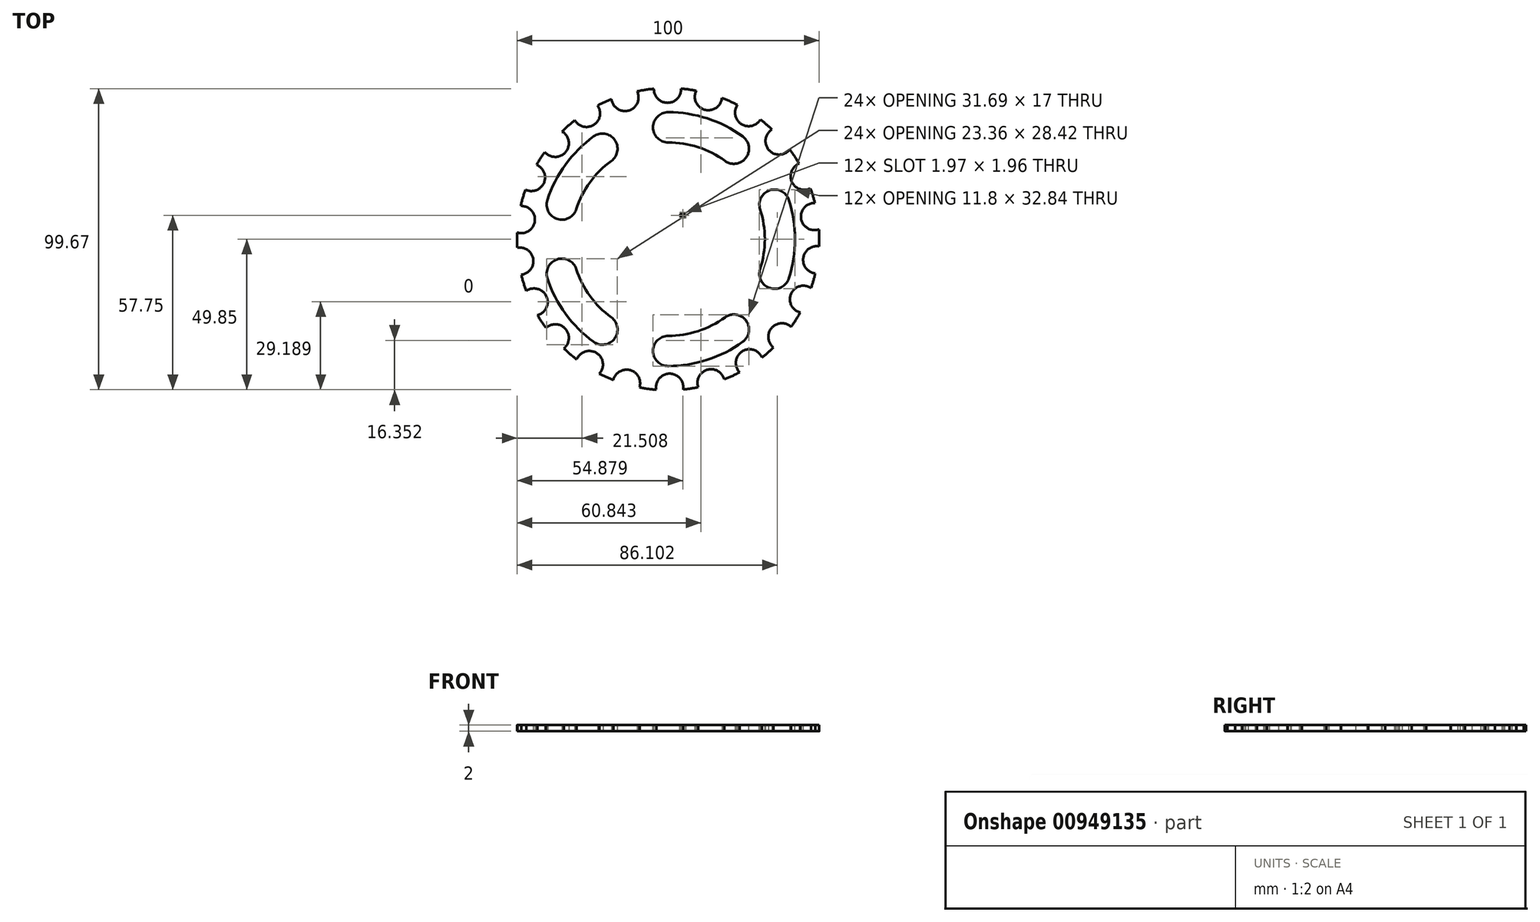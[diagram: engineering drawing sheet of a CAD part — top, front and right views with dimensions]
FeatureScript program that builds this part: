
annotation { "Feature Type Name" : "Feature", "Feature Type Description" : "" }
export const myFeature = defineFeature(function(context is Context, id is Id, definition is map)
    precondition{}
    {
        {
            var Q0;
            Q0=qCreatedBy(makeId("Top.planeOp"),FACE);
            var sketch = newSketch(context, id + "F0", { "sketchPlane" : qUnion([Q0])});
            skCircle(sketch, "E0", {"center": v(0, 0) * mm, "radius": 50 * mm});
            skArc(sketch, "E1", {"start": v(-4.73, 49.78) * mm, "mid": v(-0.2, 45.13) * mm, "end": v(4.27, 49.82) * mm});
            skArc(sketch, "E2", {"start": v(9.27, 49.13) * mm, "mid": v(12.1, 42.84) * mm, "end": v(17.8, 46.72) * mm});
            skArc(sketch, "E3.1.0", {"start": v(-18.76, 46.35) * mm, "mid": v(-12.98, 42.58) * mm, "end": v(-10.28, 48.93) * mm});
            skArc(sketch, "E3.1.1", {"start": v(-30.89, 39.32) * mm, "mid": v(-24.57, 37.86) * mm, "end": v(-23.34, 44.22) * mm});
            skArc(sketch, "E3.2.0", {"start": v(-40.84, 28.85) * mm, "mid": v(-33.94, 28.8) * mm, "end": v(-35.1, 35.6) * mm});
            skArc(sketch, "E3.2.1", {"start": v(-47.24, 16.38) * mm, "mid": v(-41.14, 18.56) * mm, "end": v(-43.54, 24.58) * mm});
            skArc(sketch, "E3.3.0", {"start": v(-49.95, 2.19) * mm, "mid": v(-44.12, 5.88) * mm, "end": v(-48.78, 10.98) * mm});
            skArc(sketch, "E3.3.1", {"start": v(-48.6, -11.76) * mm, "mid": v(-44.64, -6.63) * mm, "end": v(-49.92, -2.86) * mm});
            skArc(sketch, "E3.4.0", {"start": v(-43.2, -25.17) * mm, "mid": v(-40.3, -18.9) * mm, "end": v(-46.97, -17.14) * mm});
            skArc(sketch, "E3.4.1", {"start": v(-34.52, -36.17) * mm, "mid": v(-33.97, -29.7) * mm, "end": v(-40.45, -29.4) * mm});
            skArc(sketch, "E3.5.0", {"start": v(-22.74, -44.53) * mm, "mid": v(-23.68, -37.7) * mm, "end": v(-30.25, -39.81) * mm});
            skArc(sketch, "E3.5.1", {"start": v(-9.49, -49.1) * mm, "mid": v(-12.52, -43.36) * mm, "end": v(-18.14, -46.6) * mm});
            skArc(sketch, "E3.6.0", {"start": v(4.94, -49.75) * mm, "mid": v(0.46, -44.51) * mm, "end": v(-3.92, -49.85) * mm});
            skArc(sketch, "E3.6.1", {"start": v(18.56, -46.43) * mm, "mid": v(12.91, -43.24) * mm, "end": v(9.93, -49) * mm});
            skArc(sketch, "E3.7.0", {"start": v(31.06, -39.18) * mm, "mid": v(24.45, -37.2) * mm, "end": v(23.65, -44.05) * mm});
            skArc(sketch, "E3.7.1", {"start": v(40.71, -29.02) * mm, "mid": v(34.24, -29.4) * mm, "end": v(34.85, -35.85) * mm});
            skArc(sketch, "E3.8.0", {"start": v(47.31, -16.17) * mm, "mid": v(40.68, -18.08) * mm, "end": v(43.71, -24.28) * mm});
            skArc(sketch, "E3.8.1", {"start": v(49.94, -2.4) * mm, "mid": v(44.7, -6.22) * mm, "end": v(48.7, -11.32) * mm});
            skArc(sketch, "E3.9.0", {"start": v(48.54, 11.97) * mm, "mid": v(44, 6.79) * mm, "end": v(49.9, 3.21) * mm});
            skArc(sketch, "E3.9.1", {"start": v(43.31, 24.98) * mm, "mid": v(40.97, 18.93) * mm, "end": v(47.1, 16.8) * mm});
            skArc(sketch, "E3.10.0", {"start": v(34.36, 36.32) * mm, "mid": v(33.34, 29.5) * mm, "end": v(40.24, 29.68) * mm});
            skArc(sketch, "E3.10.1", {"start": v(22.94, 44.43) * mm, "mid": v(24.23, 38.08) * mm, "end": v(30.53, 39.6) * mm});
            skSolve(sketch);
        }
        {
            var Q0;
            {var subQ19=sQuery(id+"F0.wireOp",EDGE,"E1");Q0=makeQuery(id+"F0.imprint","IMPRINT",FACE,{"disambiguationData":[TD([[makeQuery(id+"F0.imprint","IMPRINT",EDGE,{"derivedFrom":subQ19}),-1.0]])]});}
            extrude(context, id + "F1", {"entities" : qUnion([Q0]), "depth" : 2 * mm, "offsetDistance" : 25 * mm});
        }
        {
            var Q0;
            Q0=makeQuery(id+"F1.opExtrude","CAP_FACE",FACE,{"disambiguationData":[OSD([sQuery(id+"F0.wireOp",EDGE,"E0"),sQuery(id+"F0.wireOp",EDGE,"E1"),sQuery(id+"F0.wireOp",EDGE,"E2"),sQuery(id+"F0.wireOp",EDGE,"E3.1.0"),sQuery(id+"F0.wireOp",EDGE,"E3.1.1"),sQuery(id+"F0.wireOp",EDGE,"E3.2.0"),sQuery(id+"F0.wireOp",EDGE,"E3.2.1"),sQuery(id+"F0.wireOp",EDGE,"E3.3.0"),sQuery(id+"F0.wireOp",EDGE,"E3.3.1"),sQuery(id+"F0.wireOp",EDGE,"E3.4.0"),sQuery(id+"F0.wireOp",EDGE,"E3.4.1"),sQuery(id+"F0.wireOp",EDGE,"E3.5.0"),sQuery(id+"F0.wireOp",EDGE,"E3.5.1"),sQuery(id+"F0.wireOp",EDGE,"E3.6.0"),sQuery(id+"F0.wireOp",EDGE,"E3.6.1"),sQuery(id+"F0.wireOp",EDGE,"E3.7.0"),sQuery(id+"F0.wireOp",EDGE,"E3.7.1"),sQuery(id+"F0.wireOp",EDGE,"E3.8.0"),sQuery(id+"F0.wireOp",EDGE,"E3.8.1"),sQuery(id+"F0.wireOp",EDGE,"E3.9.0"),sQuery(id+"F0.wireOp",EDGE,"E3.9.1"),sQuery(id+"F0.wireOp",EDGE,"E3.10.0"),sQuery(id+"F0.wireOp",EDGE,"E3.10.1")])],"isStart":false});
            var sketch = newSketch(context, id + "F2", { "sketchPlane" : qUnion([Q0])});
            skCircle(sketch, "E4", {"center": v(0, 0) * mm, "radius": 10 * mm});
            skArc(sketch, "E5", {"start": v(3.9, 7.55) * mm, "mid": v(4.43, 7.25) * mm, "end": v(4.94, 6.91) * mm});
            skLineSegment(sketch, "E6", {"start": v(3.9, 7.55) * mm, "end": v(4.59, 8.89) * mm});
            skLineSegment(sketch, "E7", {"start": v(4.94, 6.91) * mm, "end": v(5.86, 8.1) * mm});
            skLineSegment(sketch, "E8.1.0", {"start": v(-0.4, 8.5) * mm, "end": v(-0.47, 9.99) * mm});
            skLineSegment(sketch, "E8.1.1", {"start": v(0.82, 8.46) * mm, "end": v(1.02, 9.95) * mm});
            skArc(sketch, "E8.1.2", {"start": v(-0.4, 8.5) * mm, "mid": v(0.21, 8.5) * mm, "end": v(0.82, 8.46) * mm});
            skLineSegment(sketch, "E8.2.0", {"start": v(-4.6, 7.15) * mm, "end": v(-5.4, 8.42) * mm});
            skLineSegment(sketch, "E8.2.1", {"start": v(-3.52, 7.74) * mm, "end": v(-4.09, 9.13) * mm});
            skArc(sketch, "E8.2.2", {"start": v(-4.6, 7.15) * mm, "mid": v(-4.06, 7.47) * mm, "end": v(-3.52, 7.74) * mm});
            skLineSegment(sketch, "E8.3.0", {"start": v(-7.55, 3.9) * mm, "end": v(-8.89, 4.59) * mm});
            skLineSegment(sketch, "E8.3.1", {"start": v(-6.91, 4.94) * mm, "end": v(-8.1, 5.86) * mm});
            skArc(sketch, "E8.3.2", {"start": v(-7.55, 3.9) * mm, "mid": v(-7.25, 4.43) * mm, "end": v(-6.91, 4.94) * mm});
            skLineSegment(sketch, "E8.4.0", {"start": v(-8.5, -0.4) * mm, "end": v(-9.99, -0.47) * mm});
            skLineSegment(sketch, "E8.4.1", {"start": v(-8.46, 0.82) * mm, "end": v(-9.95, 1.02) * mm});
            skArc(sketch, "E8.4.2", {"start": v(-8.5, -0.4) * mm, "mid": v(-8.5, 0.21) * mm, "end": v(-8.46, 0.82) * mm});
            skLineSegment(sketch, "E8.5.0", {"start": v(-7.15, -4.6) * mm, "end": v(-8.42, -5.4) * mm});
            skLineSegment(sketch, "E8.5.1", {"start": v(-7.74, -3.52) * mm, "end": v(-9.13, -4.09) * mm});
            skArc(sketch, "E8.5.2", {"start": v(-7.15, -4.6) * mm, "mid": v(-7.47, -4.06) * mm, "end": v(-7.74, -3.52) * mm});
            skLineSegment(sketch, "E8.6.0", {"start": v(-3.9, -7.55) * mm, "end": v(-4.59, -8.89) * mm});
            skLineSegment(sketch, "E8.6.1", {"start": v(-4.94, -6.91) * mm, "end": v(-5.86, -8.1) * mm});
            skArc(sketch, "E8.6.2", {"start": v(-3.9, -7.55) * mm, "mid": v(-4.43, -7.25) * mm, "end": v(-4.94, -6.91) * mm});
            skLineSegment(sketch, "E8.7.0", {"start": v(0.4, -8.5) * mm, "end": v(0.47, -9.99) * mm});
            skLineSegment(sketch, "E8.7.1", {"start": v(-0.82, -8.46) * mm, "end": v(-1.02, -9.95) * mm});
            skArc(sketch, "E8.7.2", {"start": v(0.4, -8.5) * mm, "mid": v(-0.21, -8.5) * mm, "end": v(-0.82, -8.46) * mm});
            skLineSegment(sketch, "E8.8.0", {"start": v(4.6, -7.15) * mm, "end": v(5.4, -8.42) * mm});
            skLineSegment(sketch, "E8.8.1", {"start": v(3.52, -7.74) * mm, "end": v(4.09, -9.13) * mm});
            skArc(sketch, "E8.8.2", {"start": v(4.6, -7.15) * mm, "mid": v(4.06, -7.47) * mm, "end": v(3.52, -7.74) * mm});
            skLineSegment(sketch, "E8.9.0", {"start": v(7.55, -3.9) * mm, "end": v(8.89, -4.59) * mm});
            skLineSegment(sketch, "E8.9.1", {"start": v(6.91, -4.94) * mm, "end": v(8.1, -5.86) * mm});
            skArc(sketch, "E8.9.2", {"start": v(7.55, -3.9) * mm, "mid": v(7.25, -4.43) * mm, "end": v(6.91, -4.94) * mm});
            skLineSegment(sketch, "E8.10.0", {"start": v(8.5, 0.4) * mm, "end": v(9.99, 0.47) * mm});
            skLineSegment(sketch, "E8.10.1", {"start": v(8.46, -0.82) * mm, "end": v(9.95, -1.02) * mm});
            skArc(sketch, "E8.10.2", {"start": v(8.5, 0.4) * mm, "mid": v(8.5, -0.21) * mm, "end": v(8.46, -0.82) * mm});
            skLineSegment(sketch, "E8.11.0", {"start": v(7.15, 4.6) * mm, "end": v(8.42, 5.4) * mm});
            skLineSegment(sketch, "E8.11.1", {"start": v(7.74, 3.52) * mm, "end": v(9.13, 4.09) * mm});
            skArc(sketch, "E8.11.2", {"start": v(7.15, 4.6) * mm, "mid": v(7.47, 4.06) * mm, "end": v(7.74, 3.52) * mm});
            skSolve(sketch);
        }
        {
            var Q0;
            Q0=makeQuery(id+"F2.imprint","IMPRINT",FACE,{"disambiguationData":[TD([[makeQuery(id+"F2.imprint","IMPRINT",EDGE,{"derivedFrom":sQuery(id+"F2.wireOp",EDGE,"E5")}),-1.0]])]});
            extrude(context, id + "F3", {"entities" : qUnion([Q0]), "operationType" : NewBodyOperationType.REMOVE, "oppositeDirection" : true, "depth" : 2 * mm, "offsetDistance" : 25 * mm});
        }
        {
            var Q0;
            Q0=makeQuery(id+"F1.opExtrude","CAP_FACE",FACE,{"disambiguationData":[OSD([sQuery(id+"F0.wireOp",EDGE,"E0"),sQuery(id+"F0.wireOp",EDGE,"E1"),sQuery(id+"F0.wireOp",EDGE,"E2"),sQuery(id+"F0.wireOp",EDGE,"E3.1.0"),sQuery(id+"F0.wireOp",EDGE,"E3.1.1"),sQuery(id+"F0.wireOp",EDGE,"E3.2.0"),sQuery(id+"F0.wireOp",EDGE,"E3.2.1"),sQuery(id+"F0.wireOp",EDGE,"E3.3.0"),sQuery(id+"F0.wireOp",EDGE,"E3.3.1"),sQuery(id+"F0.wireOp",EDGE,"E3.4.0"),sQuery(id+"F0.wireOp",EDGE,"E3.4.1"),sQuery(id+"F0.wireOp",EDGE,"E3.5.0"),sQuery(id+"F0.wireOp",EDGE,"E3.5.1"),sQuery(id+"F0.wireOp",EDGE,"E3.6.0"),sQuery(id+"F0.wireOp",EDGE,"E3.6.1"),sQuery(id+"F0.wireOp",EDGE,"E3.7.0"),sQuery(id+"F0.wireOp",EDGE,"E3.7.1"),sQuery(id+"F0.wireOp",EDGE,"E3.8.0"),sQuery(id+"F0.wireOp",EDGE,"E3.8.1"),sQuery(id+"F0.wireOp",EDGE,"E3.9.0"),sQuery(id+"F0.wireOp",EDGE,"E3.9.1"),sQuery(id+"F0.wireOp",EDGE,"E3.10.0"),sQuery(id+"F0.wireOp",EDGE,"E3.10.1")])],"isStart":false});
            var sketch = newSketch(context, id + "F4", { "sketchPlane" : qUnion([Q0])});
            skArc(sketch, "E9", {"start": v(24.69, 33.98) * mm, "mid": v(12.98, 39.94) * mm, "end": v(0, 42) * mm});
            skArc(sketch, "E10", {"start": v(18.8, 25.89) * mm, "mid": v(9.89, 30.43) * mm, "end": v(0, 32) * mm});
            skLineSegment(sketch, "E11", {"start": v(0, 32) * mm, "end": v(0, 42) * mm, "construction": true});
            skLineSegment(sketch, "E12", {"start": v(0, 42) * mm, "end": v(0, 37) * mm, "construction": true});
            skLineSegment(sketch, "E13", {"start": v(0, 37) * mm, "end": v(5.18, 37) * mm, "construction": true});
            skCircle(sketch, "E14", {"center": v(0, 37) * mm, "radius": 5 * mm});
            skArc(sketch, "E15.1.0", {"start": v(-18.8, 25.89) * mm, "mid": v(-17.7, 32.87) * mm, "end": v(-24.69, 33.98) * mm});
            skArc(sketch, "E15.2.0", {"start": v(-39.94, 12.98) * mm, "mid": v(-36.73, 6.68) * mm, "end": v(-30.43, 9.89) * mm});
            skArc(sketch, "E15.3.0", {"start": v(-30.43, -9.89) * mm, "mid": v(-36.73, -6.68) * mm, "end": v(-39.94, -12.98) * mm});
            skArc(sketch, "E15.4.0", {"start": v(-24.69, -33.98) * mm, "mid": v(-17.7, -32.87) * mm, "end": v(-18.8, -25.89) * mm});
            skArc(sketch, "E15.5.0", {"start": v(0, -32) * mm, "mid": v(-5, -37) * mm, "end": v(0, -42) * mm});
            skArc(sketch, "E15.6.0", {"start": v(24.69, -33.98) * mm, "mid": v(25.8, -27) * mm, "end": v(18.8, -25.89) * mm});
            skArc(sketch, "E15.7.0", {"start": v(30.43, -9.89) * mm, "mid": v(33.64, -16.19) * mm, "end": v(39.94, -12.98) * mm});
            skArc(sketch, "E15.8.0", {"start": v(39.94, 12.98) * mm, "mid": v(33.64, 16.19) * mm, "end": v(30.43, 9.89) * mm});
            skArc(sketch, "E15.9.0", {"start": v(18.8, 25.89) * mm, "mid": v(25.8, 27) * mm, "end": v(24.69, 33.98) * mm});
            skArc(sketch, "E16.trimOffspring", {"start": v(30.43, -9.89) * mm, "mid": v(32, 0) * mm, "end": v(30.43, 9.89) * mm});
            skArc(sketch, "E17.trimOffspring", {"start": v(39.94, -12.98) * mm, "mid": v(42, 0) * mm, "end": v(39.94, 12.98) * mm});
            skArc(sketch, "E18.trimOffspring", {"start": v(0, -42) * mm, "mid": v(12.98, -39.94) * mm, "end": v(24.69, -33.98) * mm});
            skArc(sketch, "E19.trimOffspring", {"start": v(0, -32) * mm, "mid": v(9.89, -30.43) * mm, "end": v(18.8, -25.89) * mm});
            skArc(sketch, "E20.trimOffspring", {"start": v(-30.43, -9.89) * mm, "mid": v(-25.89, -18.8) * mm, "end": v(-18.8, -25.89) * mm});
            skArc(sketch, "E21.trimOffspring", {"start": v(-39.94, -12.98) * mm, "mid": v(-33.98, -24.69) * mm, "end": v(-24.69, -33.98) * mm});
            skArc(sketch, "E22.trimOffspring", {"start": v(-18.8, 25.89) * mm, "mid": v(-25.89, 18.8) * mm, "end": v(-30.43, 9.89) * mm});
            skArc(sketch, "E23.trimOffspring", {"start": v(-24.69, 33.98) * mm, "mid": v(-33.98, 24.69) * mm, "end": v(-39.94, 12.98) * mm});
            skSolve(sketch);
        }
        {
            var Q0;
            Q0 = qSketchRegion(id + "F4", true);
            extrude(context, id + "F5", {"entities" : qUnion([Q0]), "operationType" : NewBodyOperationType.REMOVE, "oppositeDirection" : true, "depth" : 2 * mm, "offsetDistance" : 25 * mm});
        }
    });
